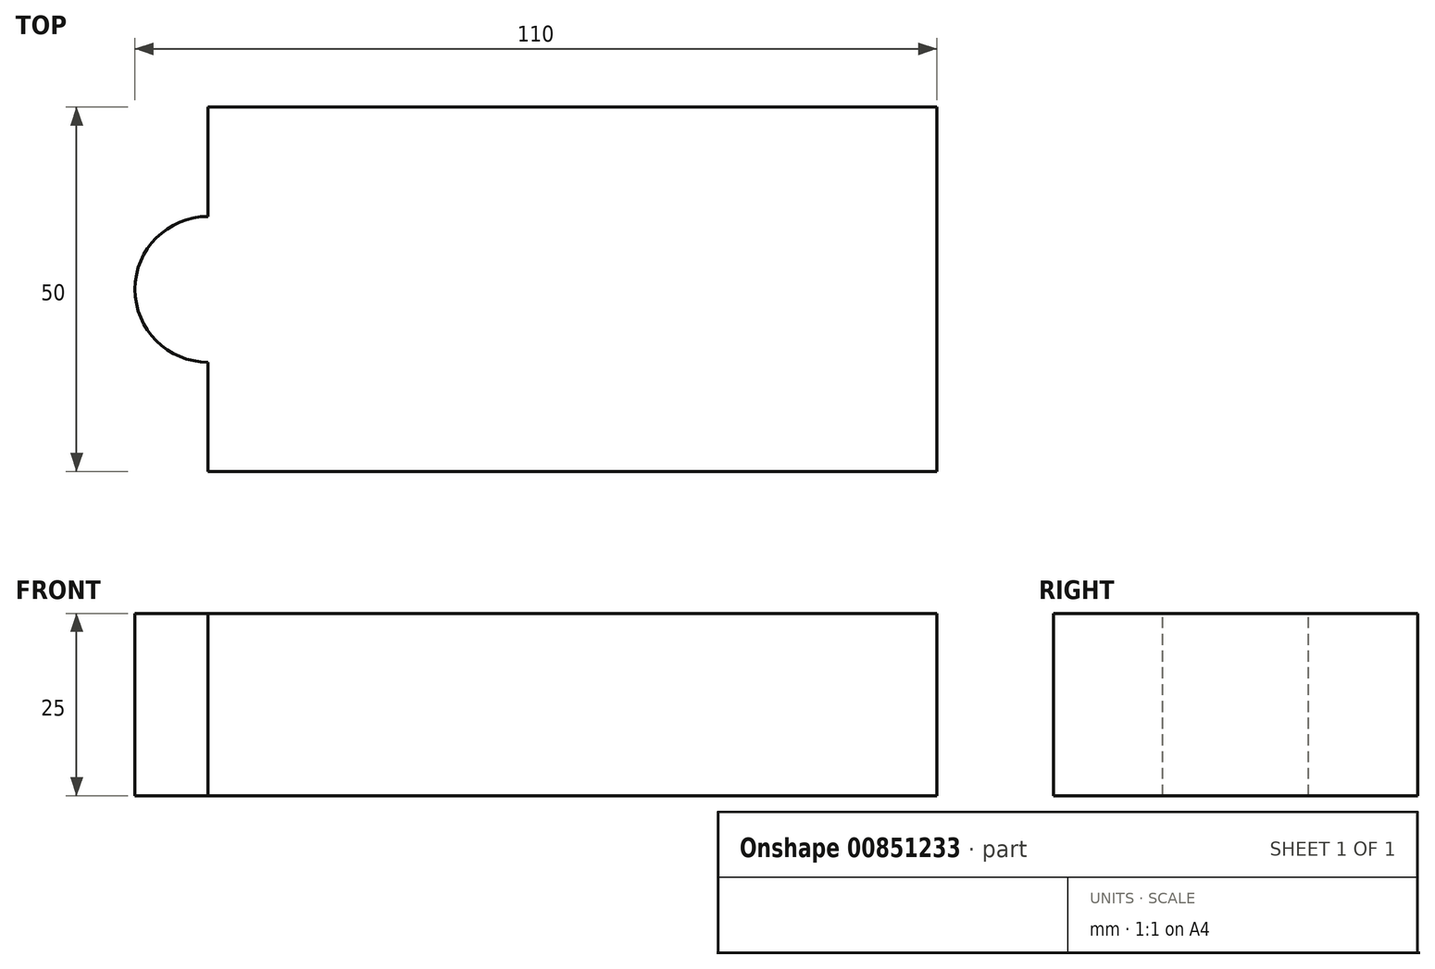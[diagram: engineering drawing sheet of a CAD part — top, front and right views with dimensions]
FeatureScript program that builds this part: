
annotation { "Feature Type Name" : "Feature", "Feature Type Description" : "" }
export const myFeature = defineFeature(function(context is Context, id is Id, definition is map)
    precondition{}
    {
        {
            var Q0;
            Q0=qCreatedBy(makeId("Top.planeOp"),FACE);
            var sketch = newSketch(context, id + "F0", { "sketchPlane" : qUnion([Q0])});
            skLineSegment(sketch, "E0.bottom", {"start": v(-50, 0) * mm, "end": v(50, 0) * mm});
            skLineSegment(sketch, "E0.top", {"start": v(-50, 50) * mm, "end": v(50, 50) * mm});
            skLineSegment(sketch, "E0.left", {"start": v(-50, 0) * mm, "end": v(-50, 50) * mm});
            skLineSegment(sketch, "E0.right", {"start": v(50, 0) * mm, "end": v(50, 50) * mm});
            skSolve(sketch);
        }
        {
            var Q0;
            Q0 = qSketchRegion(id + "F0", true);
            extrude(context, id + "F1", {"entities" : qUnion([Q0]), "depth" : 25 * mm, "offsetDistance" : 25 * mm});
        }
        {
            var Q0;
            Q0=makeQuery(id+"F1.opExtrude","CAP_FACE",FACE,{"disambiguationData":[OSD([sQuery(id+"F0.wireOp",EDGE,"E0.bottom"),sQuery(id+"F0.wireOp",EDGE,"E0.top"),sQuery(id+"F0.wireOp",EDGE,"E0.left"),sQuery(id+"F0.wireOp",EDGE,"E0.right")])],"isStart":false});
            var sketch = newSketch(context, id + "F2", { "sketchPlane" : qUnion([Q0])});
            skCircle(sketch, "E1", {"center": v(-50, 25) * mm, "radius": 10 * mm});
            skSolve(sketch);
        }
        {
            var Q0;
            Q0 = qSketchRegion(id + "F2", true);
            var Q1;
            Q1=makeQuery(id+"F1.opExtrude","CAP_FACE",FACE,{"disambiguationData":[OSD([sQuery(id+"F0.wireOp",EDGE,"E0.bottom"),sQuery(id+"F0.wireOp",EDGE,"E0.top"),sQuery(id+"F0.wireOp",EDGE,"E0.left"),sQuery(id+"F0.wireOp",EDGE,"E0.right")])],"isStart":true});
            extrude(context, id + "F3", {"entities" : qUnion([Q0]), "operationType" : NewBodyOperationType.ADD, "endBound" : BoundingType.UP_TO_SURFACE, "oppositeDirection" : true, "depth" : 25 * mm, "endBoundEntityFace" : qUnion([Q1]), "offsetDistance" : 25 * mm});
        }
    });
